# Revit family: Haworth_Epure_ExtensionDesk_AP_PRELIMINARY
name_source: partatom
category: Furniture
units: mm (PartAtom-declared; Revit-internal decimal feet)

## family parameters
Always vertical = Yes
Cut with Voids When Loaded = No
OmniClass Number = 23.40.70.14.64.11
OmniClass Title = Office Furniture
Room Calculation Point = No
Shared = No
Work Plane-Based = No

## types (4) — shared parameters
Actual Depth = 300 mm
Actual Height = 730 mm  [stored 2.39501 ft]
Assembly Code = E2020200
Description = Haworth - Epure -Extension Desk
Leg Height = 695 mm  [stored 2.28018 ft]
Manufacturer = Haworth
Model = SYEPED1X03
Revision Number = 1
Size = Verify Final Dim.w/ Haworth
Trim Finish = Haworth _ Metal _ Structured White EC
URL = https://www.haworth.com
URL - Product = https://www.haworth.com
Warranty = http://www.haworth.com
Worksurface Depth = 300 mm
Worksurface Width = 1400, 1500, 1600, 180 mm

## per-type parameters (varying)
| type | Actual Width | Aluminium Legs | Wooden Legs |
| 1800 x 300 | 1800 mm  [stored 5.90551 ft] | No | Yes |
| 1600 x 300 | 1600 mm  [stored 5.24934 ft] | Yes | No |
| 1500 x 300 | 1500 mm  [stored 4.92126 ft] | No | Yes |
| 1400 x 300 | 1400 mm  [stored 4.59318 ft] | Yes | No |

note: [stored X ft] marks values corroborated as IEEE doubles in the binary element streams (Revit-internal decimal feet)

## geometry (parser evidence)
native form markers: Sweep x14
no freeform markers — native parametric forms only
